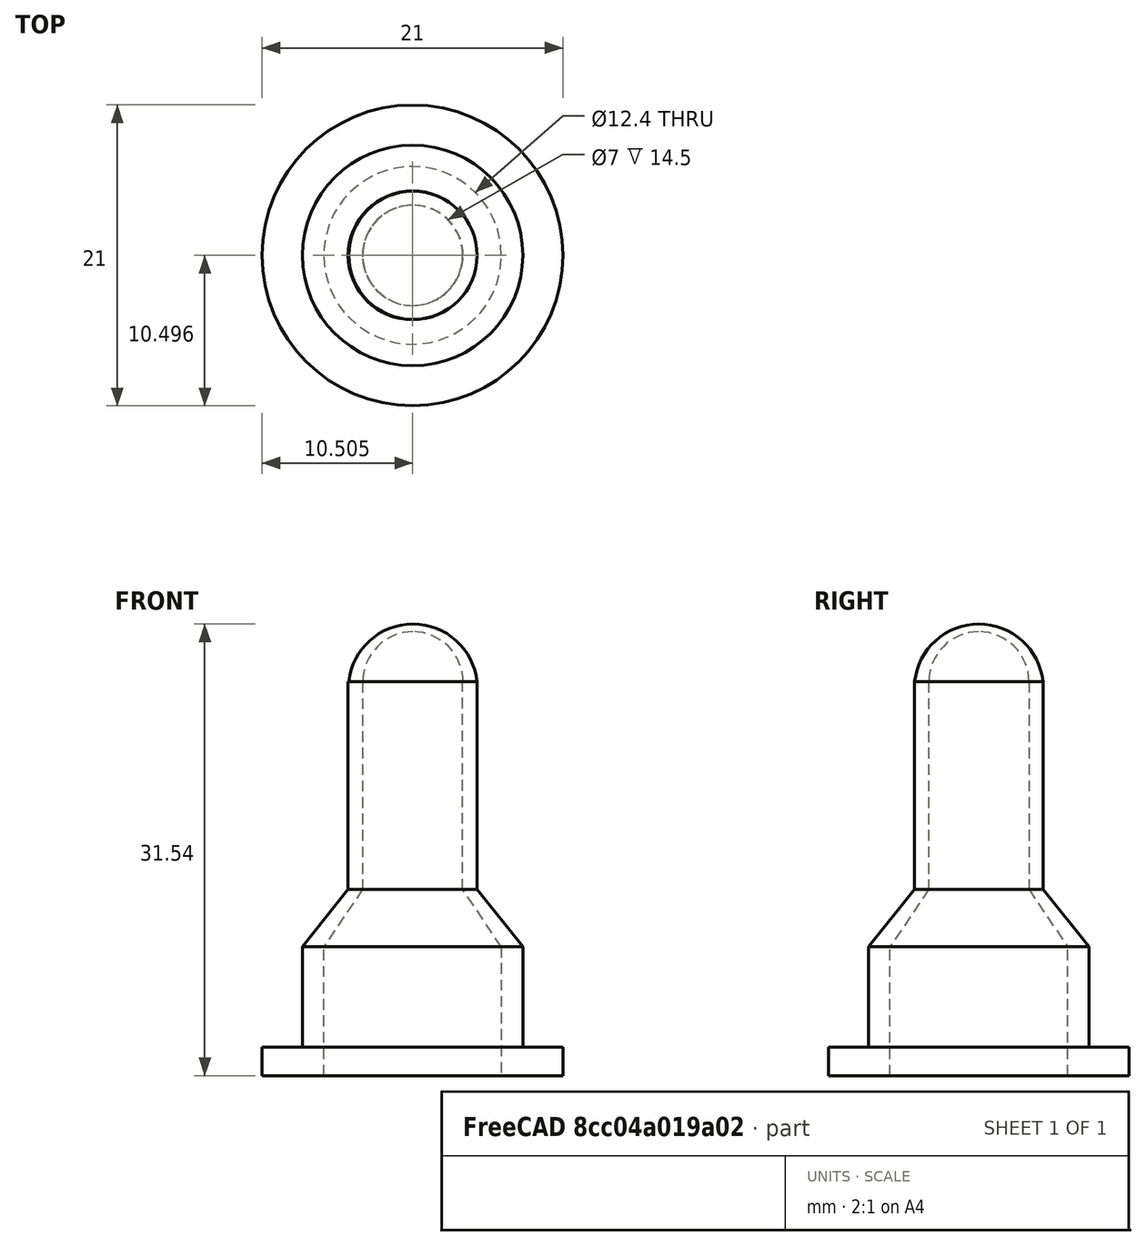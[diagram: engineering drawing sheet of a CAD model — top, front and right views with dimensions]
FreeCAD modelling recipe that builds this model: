
FCSTD DOCUMENT  (FreeCAD 0.20R29177 +233 (Git))
Label: TetoKupak
License: All rights reserved
LicenseURL: http://en.wikipedia.org/wiki/All_rights_reserved
objects: Part::Part2DObjectPython×10, Part::Extrusion×8, Part::Cut×6, Part::MultiFuse×6, Part::FeaturePython×6, Part::Cone×3, Part::Feature×3, App::DocumentObjectGroup×2
note: 42 computed .brp shape members not serialized (recipe doc carries the construction recipe); baked Part::Feature solids carry a one-line shape summary decoded from their .brp

FEATURE [Part::Part2DObjectPython] Circle  # Draft 2D object (typed FeaturePython)
  Area = 346.361
  FirstAngle = 0
  LastAngle = 0
  MakeFace = true
  Placement = pos=(-1.75538,-3.11438,0) rot=(0,0,1;0rad)
  Radius = 10.5
FEATURE [Part::Extrusion] Extrusion
  Base = -> Circle
  Dir = (0,0,2)
  DirMode = 0
  FaceMakerClass = Part::FaceMakerBullseye
  LengthFwd = 0
  LengthRev = 0
  Solid = true
  Symmetric = false
FEATURE [Part::Part2DObjectPython] Circle001  # Draft 2D object (typed FeaturePython)
  Area = 186.265
  FirstAngle = 0
  LastAngle = 0
  MakeFace = true
  Placement = pos=(-1.75538,-3.11438,2) rot=(0,0,1;0rad)
  Radius = 7.7
FEATURE [Part::Extrusion] Extrusion001
  Base = -> Circle001
  Dir = (0,0,7)
  DirMode = 0
  FaceMakerClass = Part::FaceMakerBullseye
  LengthFwd = 0
  LengthRev = 0
  Solid = true
  Symmetric = false
FEATURE [Part::Part2DObjectPython] Circle002  # Draft 2D object (typed FeaturePython)
  Area = 63.6173
  FirstAngle = 0
  LastAngle = 0
  MakeFace = true
  Placement = pos=(-1.75538,-3.11438,9) rot=(0,0,1;0rad)
  Radius = 4.5
FEATURE [Part::Extrusion] Extrusion002
  Base = -> Circle002
  Dir = (0,0,18.5)
  DirMode = 0
  FaceMakerClass = Part::FaceMakerBullseye
  LengthFwd = 0
  LengthRev = 0
  Solid = true
  Symmetric = false
FEATURE [Part::Cone] Cone
  Angle = 360
  AttacherType = Attacher::AttachEngine3D
  Height = 4
  Placement = pos=(2.74462,-3.11438,17.5) rot=(0,0,1;0rad)
  Radius1 = 7.7
  Radius2 = 4.5
FEATURE [Part::Cone] Cone001
  Angle = 360
  AttacherType = Attacher::AttachEngine3D
  Height = 4
  Placement = pos=(2.74462,-3.11438,17.5) rot=(0,0,1;0rad)
  Radius1 = 6.2
  Radius2 = 3
FEATURE [Part::Cut] Cut
  Base = -> Cone
  Placement = pos=(-4.5,3.1e-15,-8.5) rot=(0,0,1;0rad)
  Tool = -> Cone001
FEATURE [Part::MultiFuse] Fusion
  Shapes = -> [Extrusion002,Extrusion001,Extrusion]
FEATURE [Part::Part2DObjectPython] Circle003  # Draft 2D object (typed FeaturePython)
  Area = 28.2743
  FirstAngle = 0
  LastAngle = 0
  MakeFace = true
  Placement = pos=(-1.75538,-3.11438,27.5) rot=(0,0,1;0rad)
  Radius = 3
FEATURE [Part::Extrusion] Extrusion003
  Base = -> Circle003
  Dir = (0,0,-43.9081)
  DirMode = 0
  FaceMakerClass = Part::FaceMakerBullseye
  LengthFwd = 0
  LengthRev = 0
  Solid = true
  Symmetric = false
FEATURE [Part::Cut] Cut001
  Base = -> Fusion
  Tool = -> Extrusion003
FEATURE [Part::MultiFuse] Fusion001
  Shapes = -> [Cut,Cut001]
FEATURE [Part::Feature] Face
  shape: bbox 9 x 9 x 2e-07 mm, 1 faces, 0 solids (baked)
FEATURE [Part::Part2DObjectPython] Rectangle  # Draft 2D object (typed FeaturePython)
  Area = 1573.32
  ChamferSize = 0
  Columns = 1
  FilletRadius = 0
  Height = 52.3808
  Length = 30.0361
  MakeFace = true
  Placement = pos=(9.2204,26.2786,9) rot=(0,0,1;3.14159rad)
  Rows = 1
FEATURE [Part::FeaturePython] Slice  # WARN: FeaturePython — macro-defined, semantics opaque (R4)
  Base = -> Fusion001
  Mode = 1
  Tolerance = 0
  Tools = -> [Rectangle]
FEATURE [Part::FeaturePython] Slice_child0  label="Slice.0"  # WARN: FeaturePython — macro-defined, semantics opaque (R4)
  Base = -> Slice
  FilterType = 1
  Invert = false
  OverrideMaxVal = 0
  WindowFrom = 80
  WindowTo = 100
  items = 0
FEATURE [Part::FeaturePython] Slice_child1  label="Slice.1"  # WARN: FeaturePython — macro-defined, semantics opaque (R4)
  Base = -> Slice
  FilterType = 1
  Invert = false
  OverrideMaxVal = 0
  WindowFrom = 80
  WindowTo = 100
  items = 1
FEATURE [Part::Part2DObjectPython] Rectangle001  # Draft 2D object (typed FeaturePython)
  Area = 1569.46
  ChamferSize = 0
  Columns = 1
  FilletRadius = 0
  Height = 51.2405
  Length = 30.6293
  MakeFace = true
  Placement = pos=(11.1619,26.3625,13) rot=(0,0,1;3.14159rad)
  Rows = 1
FEATURE [Part::FeaturePython] Slice001  # WARN: FeaturePython — macro-defined, semantics opaque (R4)
  Base = -> Slice_child0
  Mode = 1
  Tolerance = 0
  Tools = -> [Rectangle001]
FEATURE [App::DocumentObjectGroup] GrExplode_Slice001  label="Exploded Slice001"
FEATURE [Part::FeaturePython] Slice001_child0  label="Slice001.0"  # WARN: FeaturePython — macro-defined, semantics opaque (R4)
  Base = -> Slice001
  FilterType = 1
  Invert = false
  OverrideMaxVal = 0
  Placement = pos=(-33.3877,-24.7335,0) rot=(0,0,1;0rad)
  WindowFrom = 80
  WindowTo = 100
  items = 0
FEATURE [Part::FeaturePython] Slice001_child1  label="Slice001.1"  # WARN: FeaturePython — macro-defined, semantics opaque (R4)
  Base = -> Slice001
  FilterType = 1
  Invert = false
  OverrideMaxVal = 0
  WindowFrom = 80
  WindowTo = 100
  items = 1
FEATURE [Part::Feature] Face001
  Placement = pos=(-33.3877,-24.7335,0) rot=(0,0,1;0rad)
  shape: bbox 9 x 9 x 2e-07 mm, 1 faces, 0 solids (baked)
FEATURE [Part::Extrusion] Extrusion004
  Base = -> Face001
  Dir = (0,0,43.2268)
  DirMode = 0
  FaceMakerClass = Part::FaceMakerBullseye
  LengthFwd = 0
  LengthRev = 0
  Solid = true
  Symmetric = false
FEATURE [Part::Cut] Cut002
  Base = -> Slice001_child0
  Tool = -> Extrusion004
FEATURE [Part::Cone] Cone002
  Angle = 360
  AttacherType = Attacher::AttachEngine3D
  Height = 4
  Placement = pos=(-35.1431,-27.8479,9) rot=(0,0,1;0rad)
  Radius1 = 6.2
  Radius2 = 3.5
FEATURE [Part::Part2DObjectPython] Line  # Draft 2D object (typed FeaturePython)
  Area = 0
  ChamferSize = 0
  Closed = false
  End = (-39.6431,-27.8479,13)
  FilletRadius = 0
  Length = 9
  MakeFace = true
  Placement = pos=(-30.6431,-27.8479,13) rot=(1,0,0;3.14159rad)
  Points = (2) [(0,0,0),(-9,0,0)]
  Start = (-30.6431,-27.8479,13)
  Subdivisions = 0
FEATURE [Part::Part2DObjectPython] Circle004  # Draft 2D object (typed FeaturePython)
  Area = 63.6173
  FirstAngle = 0
  LastAngle = 0
  MakeFace = true
  Placement = pos=(-35.1431,-27.8479,13) rot=(1,0,0;3.14159rad)
  Radius = 4.5
FEATURE [Part::Extrusion] Extrusion005
  Base = -> Circle004
  Dir = (0,0,-1.875)
  DirMode = 0
  FaceMakerClass = Part::FaceMakerBullseye
  LengthFwd = 0
  LengthRev = 0
  Solid = true
  Symmetric = false
FEATURE [Part::MultiFuse] Fusion002
  Shapes = -> [Cut002,Extrusion005]
FEATURE [Part::Cut] Cut003
  Base = -> Fusion002
  Placement = pos=(33.3877,24.7335,0) rot=(0,0,1;0rad)
  Tool = -> Cone002
FEATURE [Part::Part2DObjectPython] Circle005  # Draft 2D object (typed FeaturePython)
  Area = 38.4845
  FirstAngle = 0
  LastAngle = 0
  MakeFace = true
  Placement = pos=(-1.75538,-3.11438,13) rot=(1,0,0;3.14159rad)
  Radius = 3.5
FEATURE [Part::Extrusion] Extrusion006
  Base = -> Circle005
  Dir = (0,0,25.1488)
  DirMode = 0
  FaceMakerClass = Part::FaceMakerBullseye
  LengthFwd = 0
  LengthRev = 0
  Solid = true
  Symmetric = false
FEATURE [Part::Cut] Cut004
  Base = -> Slice001_child1
  Tool = -> Extrusion006
FEATURE [Part::MultiFuse] Fusion003
  Shapes = -> [Cut004,Cut003]
FEATURE [Part::Part2DObjectPython] Circle006  # Draft 2D object (typed FeaturePython)
  Area = 120.763
  FirstAngle = 0
  LastAngle = 0
  MakeFace = true
  Placement = pos=(-1.75538,-3.11438,9) rot=(0,0,1;0rad)
  Radius = 6.2
FEATURE [Part::Extrusion] Extrusion007
  Base = -> Circle006
  Dir = (0,0,-29.434)
  DirMode = 0
  FaceMakerClass = Part::FaceMakerBullseye
  LengthFwd = 0
  LengthRev = 0
  Solid = true
  Symmetric = false
FEATURE [Part::Cut] Cut005
  Base = -> Slice_child1
  Tool = -> Extrusion007
FEATURE [Part::MultiFuse] Fusion004
  Shapes = -> [Fusion003,Cut005]
FEATURE [Part::Feature] Cut006
  shape: bbox 8.954 x 8.954 x 4.044 mm, 3 faces (baked)
FEATURE [Part::MultiFuse] Fusion005
  Shapes = -> [Fusion004,Cut006]
FEATURE [App::DocumentObjectGroup] GrExplode_Slice  label="Exploded Slice"
  Group = -> [Slice_child0,Fusion005]
